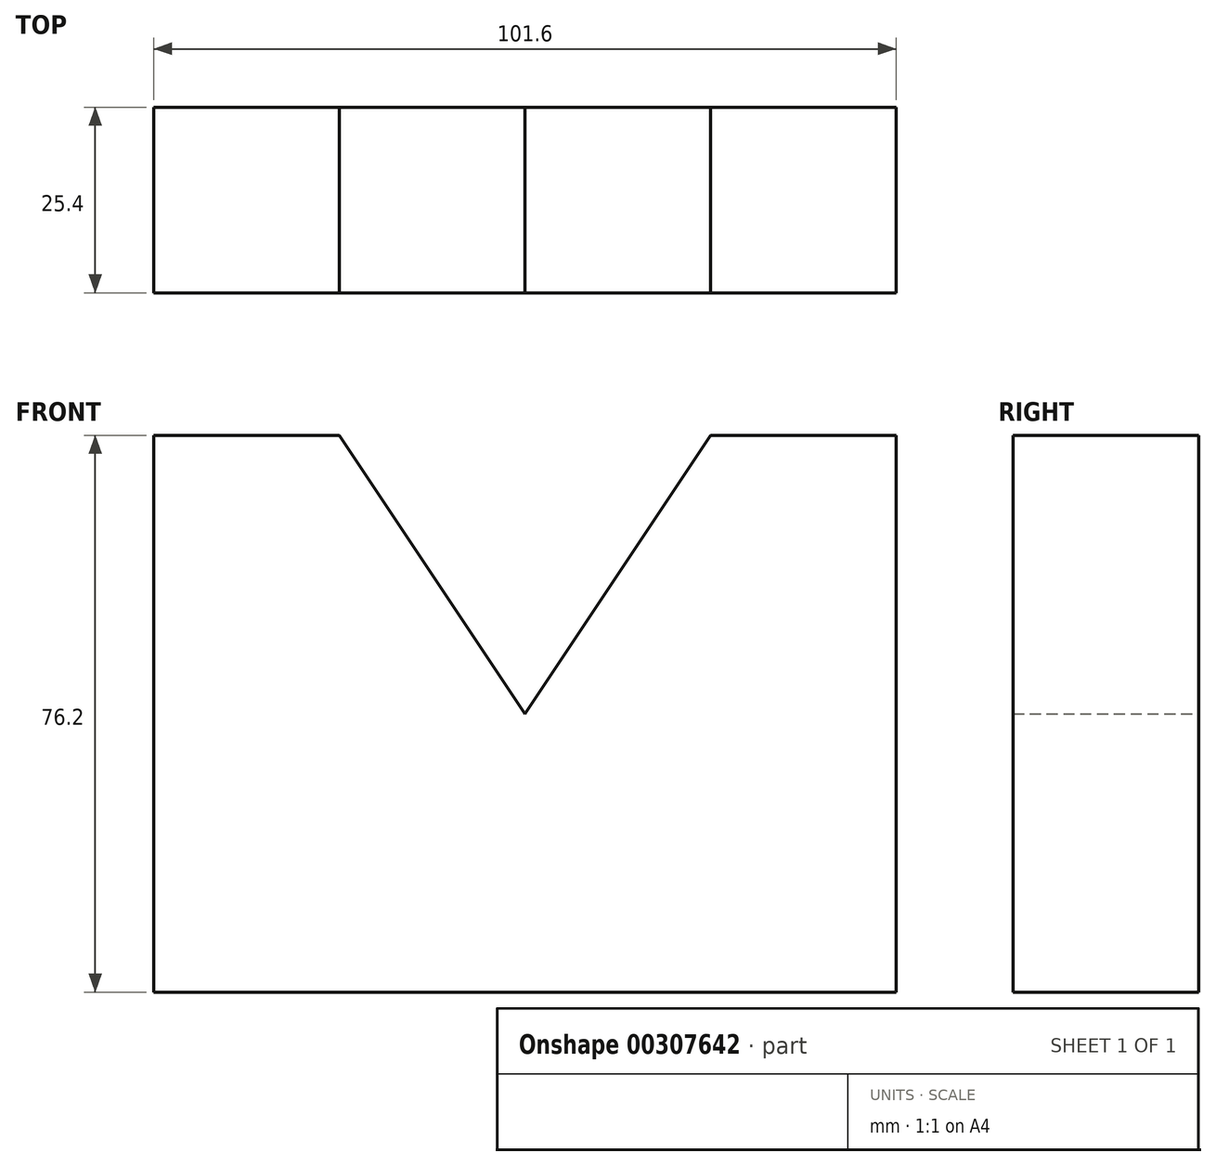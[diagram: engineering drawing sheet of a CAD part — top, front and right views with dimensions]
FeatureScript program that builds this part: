
annotation { "Feature Type Name" : "Feature", "Feature Type Description" : "" }
export const myFeature = defineFeature(function(context is Context, id is Id, definition is map)
    precondition{}
    {
        {
            var Q0;
            Q0=qCreatedBy(makeId("Front.planeOp"),FACE);
            var sketch = newSketch(context, id + "F0", { "sketchPlane" : qUnion([Q0])});
            skLineSegment(sketch, "E0", {"start": v(-61.18, -53.68) * mm, "end": v(40.42, -53.68) * mm});
            skLineSegment(sketch, "E1", {"start": v(40.42, -53.68) * mm, "end": v(40.42, 22.52) * mm});
            skLineSegment(sketch, "E2", {"start": v(-61.18, -53.68) * mm, "end": v(-61.18, 22.52) * mm});
            skLineSegment(sketch, "E3", {"start": v(-61.18, 22.52) * mm, "end": v(-35.78, 22.52) * mm});
            skLineSegment(sketch, "E4", {"start": v(40.42, 22.52) * mm, "end": v(15.02, 22.52) * mm});
            skLineSegment(sketch, "E5", {"start": v(-35.78, 22.52) * mm, "end": v(-10.38, -15.58) * mm});
            skLineSegment(sketch, "E6", {"start": v(15.02, 22.52) * mm, "end": v(-10.38, -15.58) * mm});
            skSolve(sketch);
        }
        {
            var Q0;
            Q0=makeQuery(id+"F0.imprint","IMPRINT",FACE,{"disambiguationData":[TD([[makeQuery(id+"F0.imprint","IMPRINT",EDGE,{"derivedFrom":sQuery(id+"F0.wireOp",EDGE,"E0")}),1.0]])]});
            extrude(context, id + "F1", {"entities" : qUnion([Q0]), "depth" : 25.4 * mm});
        }
    });
